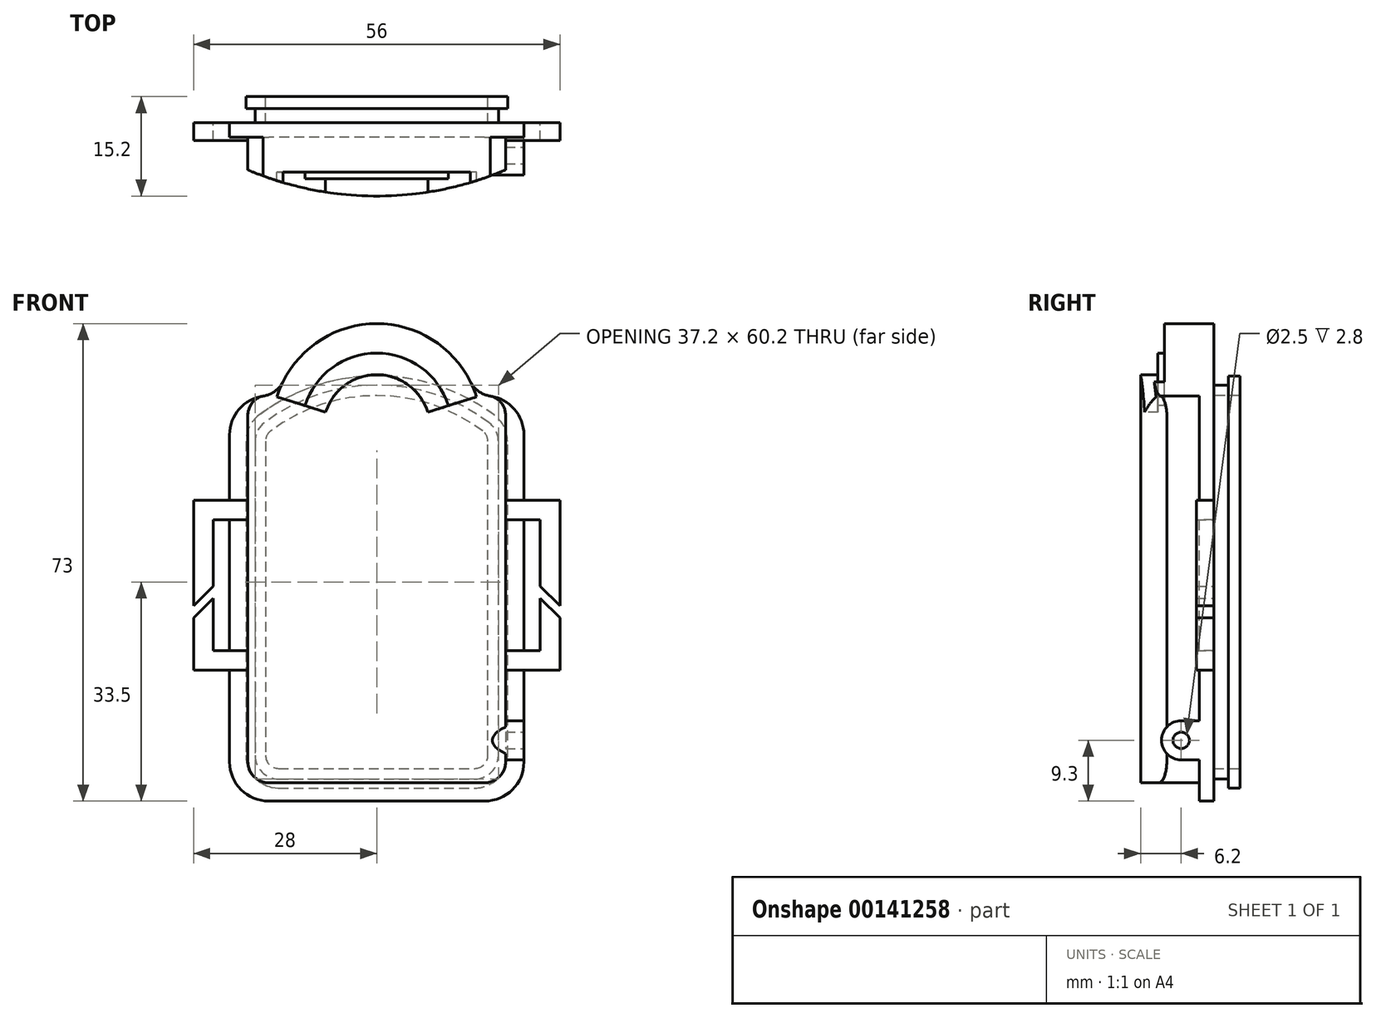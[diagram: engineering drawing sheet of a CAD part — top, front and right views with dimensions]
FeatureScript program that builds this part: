
annotation { "Feature Type Name" : "Feature", "Feature Type Description" : "" }
export const myFeature = defineFeature(function(context is Context, id is Id, definition is map)
    precondition{}
    {
        {
            var Q0;
            Q0=qCreatedBy(makeId("Front.planeOp"),FACE);
            var sketch = newSketch(context, id + "F0", { "sketchPlane" : qUnion([Q0])});
            skLineSegment(sketch, "E0.bottom", {"start": v(22.5, -57) * mm, "end": v(-22.5, -57) * mm});
            skLineSegment(sketch, "E0.top", {"start": v(22.5, 5) * mm, "end": v(-22.5, 5) * mm});
            skLineSegment(sketch, "E0.left", {"start": v(22.5, -57) * mm, "end": v(22.5, 5) * mm});
            skLineSegment(sketch, "E0.right", {"start": v(-22.5, -57) * mm, "end": v(-22.5, 5) * mm});
            skPoint(sketch, "E0.middle", {"position": v(0, -26) * mm});
            skArc(sketch, "E1", {"start": v(15.2, 5) * mm, "mid": v(0, 16) * mm, "end": v(-15.2, 5) * mm});
            skSolve(sketch);
        }
        {
            var Q0;
            Q0 = qSketchRegion(id + "F0", true);
            extrude(context, id + "F1", {"entities" : qUnion([Q0]), "depth" : 2.2 * mm});
        }
        {
            var Q0;
            Q0=makeQuery(id+"F1.opExtrude","SWEPT_EDGE",EDGE,{"disambiguationData":[OSD([sQuery(id+"F0.wireOp",EDGE,"E0.top"),sQuery(id+"F0.wireOp",EDGE,"E0.right")])]});
            var Q1;
            Q1=makeQuery(id+"F1.opExtrude","SWEPT_EDGE",EDGE,{"disambiguationData":[OSD([sQuery(id+"F0.wireOp",EDGE,"E0.top"),sQuery(id+"F0.wireOp",EDGE,"E0.left")])]});
            var Q2;
            Q2=makeQuery(id+"F1.opExtrude","SWEPT_EDGE",EDGE,{"disambiguationData":[OSD([sQuery(id+"F0.wireOp",EDGE,"E0.bottom"),sQuery(id+"F0.wireOp",EDGE,"E0.right")])]});
            var Q3;
            Q3=makeQuery(id+"F1.opExtrude","SWEPT_EDGE",EDGE,{"disambiguationData":[OSD([sQuery(id+"F0.wireOp",EDGE,"E0.bottom"),sQuery(id+"F0.wireOp",EDGE,"E0.left")])]});
            fillet(context, id + "F2", {"entities" : qUnion([Q0, Q1, Q2, Q3]), "radius" : 6 * mm, "allowEdgeOverflow" : false});
        }
        {
            var Q0;
            {var subQ0=sQuery(id+"F0.wireOp",EDGE,"E1");var subQ1=sQuery(id+"F0.wireOp",EDGE,"E0.top");Q0=makeQuery(id+"F1.opExtrude","SWEPT_EDGE",EDGE,{"disambiguationData":[OSD([subQ1,subQ0]),TDD([makeQuery(id+"F0.imprint","INTERSECT",VERTEX,{"disambiguationData":[OD(1.0)],"derivedFrom":[subQ1,subQ0]})])]});}
            var Q1;
            {var subQ0=sQuery(id+"F0.wireOp",EDGE,"E1");var subQ1=sQuery(id+"F0.wireOp",EDGE,"E0.top");Q1=makeQuery(id+"F1.opExtrude","SWEPT_EDGE",EDGE,{"disambiguationData":[OSD([subQ1,subQ0]),TDD([makeQuery(id+"F0.imprint","INTERSECT",VERTEX,{"disambiguationData":[OD(0.0)],"derivedFrom":[subQ1,subQ0]})])]});}
            fillet(context, id + "F3", {"entities" : qUnion([Q0, Q1]), "radius" : 4 * mm, "tangentPropagation" : true, "allowEdgeOverflow" : false});
        }
        {
            var Q0;
            Q0=makeQuery(id+"F1.opExtrude","CAP_FACE",FACE,{"disambiguationData":[OSD([sQuery(id+"F0.wireOp",EDGE,"E0.bottom"),sQuery(id+"F0.wireOp",EDGE,"E0.top"),sQuery(id+"F0.wireOp",EDGE,"E0.left"),sQuery(id+"F0.wireOp",EDGE,"E0.right"),sQuery(id+"F0.wireOp",EDGE,"E1")])],"isStart":false});
            var sketch = newSketch(context, id + "F4", { "sketchPlane" : qUnion([Q0])});
            skArc(sketch, "E2.0", {"start": v(22.5, -1) * mm, "mid": v(21.03, 2.93) * mm, "end": v(17.35, 4.94) * mm});
            skArc(sketch, "E3.0", {"start": v(-17.35, 4.94) * mm, "mid": v(-21.03, 2.93) * mm, "end": v(-22.5, -1) * mm});
            skArc(sketch, "E4.0", {"start": v(-14.33, 7.12) * mm, "mid": v(-15.57, 5.66) * mm, "end": v(-17.35, 4.94) * mm});
            skArc(sketch, "E5.0", {"start": v(14.33, 7.12) * mm, "mid": v(0, 16) * mm, "end": v(-14.33, 7.12) * mm});
            skArc(sketch, "E6.0", {"start": v(17.35, 4.94) * mm, "mid": v(15.57, 5.66) * mm, "end": v(14.33, 7.12) * mm});
            skLineSegment(sketch, "E7.0", {"start": v(-19.7, -51) * mm, "end": v(-19.7, 2.01) * mm});
            skLineSegment(sketch, "E7.1", {"start": v(19.7, -51) * mm, "end": v(19.7, 2.01) * mm});
            skArc(sketch, "E7.2", {"start": v(16.5, -54.2) * mm, "mid": v(18.76, -53.26) * mm, "end": v(19.7, -51) * mm});
            skLineSegment(sketch, "E7.3", {"start": v(16.5, -54.2) * mm, "end": v(-16.5, -54.2) * mm});
            skArc(sketch, "E7.4", {"start": v(-19.7, -51) * mm, "mid": v(-18.76, -53.26) * mm, "end": v(-16.5, -54.2) * mm});
            skArc(sketch, "E8", {"start": v(-19.7, 2.01) * mm, "mid": v(-19.04, 3.89) * mm, "end": v(-17.35, 4.94) * mm});
            skArc(sketch, "E9.MirrorCS", {"start": v(19.7, 2.01) * mm, "mid": v(19.04, 3.89) * mm, "end": v(17.35, 4.94) * mm});
            skSolve(sketch);
        }
        {
            var Q0;
            Q0=makeQuery(id+"F4.imprint","IMPRINT",FACE,{"disambiguationData":[TD([[makeQuery(id+"F4.imprint","IMPRINT",EDGE,{"derivedFrom":sQuery(id+"F4.wireOp",EDGE,"E4.0")}),1.0]])]});
            extrude(context, id + "F5", {"entities" : qUnion([Q0]), "operationType" : NewBodyOperationType.ADD, "depth" : 10 * mm});
        }
        {
            var Q0;
            Q0=qCreatedBy(makeId("Top.planeOp"),FACE);
            var sketch = newSketch(context, id + "F6", { "sketchPlane" : qUnion([Q0])});
            skLineSegment(sketch, "E10.0", {"start": v(19.7, -12.2) * mm, "end": v(19.7, -7.2) * mm});
            skLineSegment(sketch, "E11.0", {"start": v(-19.7, -12.2) * mm, "end": v(-19.7, -7.2) * mm});
            skArc(sketch, "E12", {"start": v(-19.7, -7.2) * mm, "mid": v(0, -11.2) * mm, "end": v(19.7, -7.2) * mm});
            skLineSegment(sketch, "E13", {"start": v(-19.7, -12.2) * mm, "end": v(19.7, -12.2) * mm});
            skPoint(sketch, "E14.orphan", {"position": v(-19.7, -2.2) * mm});
            skPoint(sketch, "E15.orphan", {"position": v(19.7, -2.2) * mm});
            skSolve(sketch);
        }
        {
            var Q0;
            Q0=makeQuery(id+"F6.imprint","IMPRINT",FACE,{"disambiguationData":[TD([[makeQuery(id+"F6.imprint","IMPRINT",EDGE,{"derivedFrom":sQuery(id+"F6.wireOp",EDGE,"E10.0")}),1.0]])]});
            extrude(context, id + "F7", {"entities" : qUnion([Q0]), "operationType" : NewBodyOperationType.REMOVE, "endBound" : BoundingType.THROUGH_ALL, "oppositeDirection" : true, "depth" : 25 * mm, "hasSecondDirection" : true, "secondDirectionBound" : SecondDirectionBoundingType.THROUGH_ALL, "secondDirectionOppositeDirection" : false, "secondDirectionDepth" : 25 * mm});
        }
        {
            var Q0;
            Q0=qCreatedBy(makeId("Right.planeOp"),FACE);
            var sketch = newSketch(context, id + "F8", { "sketchPlane" : qUnion([Q0])});
            skLineSegment(sketch, "E16", {"start": v(-11.2, 16) * mm, "end": v(0, 16) * mm});
            skLineSegment(sketch, "E17", {"start": v(-11.2, -54.2) * mm, "end": v(-11.2, 16) * mm});
            skLineSegment(sketch, "E18", {"start": v(-7.55, 16) * mm, "end": v(-7.55, 11.5) * mm});
            skLineSegment(sketch, "E19", {"start": v(-7.55, 11.5) * mm, "end": v(-8.55, 11.5) * mm});
            skLineSegment(sketch, "E20", {"start": v(-8.55, 11.5) * mm, "end": v(-8.55, 8.2) * mm});
            skLineSegment(sketch, "E21", {"start": v(-8.55, 8.2) * mm, "end": v(-11.2, 8.2) * mm});
            skLineSegment(sketch, "E22", {"start": v(-11.2, 16) * mm, "end": v(-11.2, 8.2) * mm});
            skLineSegment(sketch, "E23", {"start": v(0, 0) * mm, "end": v(-11.2, 0) * mm, "construction": true});
            skSolve(sketch);
        }
        {
            var Q0;
            {var subQ0=sQuery(id+"F8.wireOp",EDGE,"E18");Q0=makeQuery(id+"F8.imprint","IMPRINT",FACE,{"disambiguationData":[TD([[makeQuery(id+"F8.imprint","IMPRINT",EDGE,{"derivedFrom":subQ0}),-1.0]])]});}
            var Q1;
            Q1=sQuery(id+"F8.wireOp",EDGE,"E23");
            revolve(context, id + "F9", {"operationType" : NewBodyOperationType.REMOVE, "entities" : qUnion([Q0]), "axis" : qUnion([Q1]), "revolveType" : RevolveType.SYMMETRIC, "oppositeDirection" : true, "angle" : 145 * degree});
        }
        {
            var Q0;
            Q0=qCreatedBy(makeId("Front.planeOp"),FACE);
            var sketch = newSketch(context, id + "F10", { "sketchPlane" : qUnion([Q0])});
            skLineSegment(sketch, "E24.bottom", {"start": v(19.7, -11) * mm, "end": v(28, -11) * mm});
            skLineSegment(sketch, "E24.top", {"start": v(19.7, -37) * mm, "end": v(28, -37) * mm});
            skLineSegment(sketch, "E24.left", {"start": v(19.7, -11) * mm, "end": v(19.7, -14) * mm});
            skLineSegment(sketch, "E24.right", {"start": v(28, -11) * mm, "end": v(28, -27.16) * mm});
            skLineSegment(sketch, "E25.0", {"start": v(19.7, -34) * mm, "end": v(25, -34) * mm});
            skLineSegment(sketch, "E25.1", {"start": v(25, -14) * mm, "end": v(25, -24.16) * mm});
            skLineSegment(sketch, "E25.2", {"start": v(19.7, -14) * mm, "end": v(25, -14) * mm});
            skLineSegment(sketch, "E26", {"start": v(25, -26) * mm, "end": v(28, -29) * mm});
            skLineSegment(sketch, "E27", {"start": v(25, -24.16) * mm, "end": v(28, -27.16) * mm});
            skLineSegment(sketch, "E28.trimOffspring", {"start": v(19.7, -34) * mm, "end": v(19.7, -37) * mm});
            skLineSegment(sketch, "E29.trimOffspring", {"start": v(25, -26) * mm, "end": v(25, -34) * mm});
            skLineSegment(sketch, "E30.trimOffspring", {"start": v(28, -29) * mm, "end": v(28, -37) * mm});
            skLineSegment(sketch, "E31.MirrorCS", {"start": v(-19.7, -11) * mm, "end": v(-19.7, -14) * mm});
            skLineSegment(sketch, "E32.MirrorCS", {"start": v(-25, -24.16) * mm, "end": v(-28, -27.16) * mm});
            skLineSegment(sketch, "E33.MirrorCS", {"start": v(-19.7, -37) * mm, "end": v(-28, -37) * mm});
            skLineSegment(sketch, "E34.MirrorCS", {"start": v(-28, -11) * mm, "end": v(-28, -27.16) * mm});
            skLineSegment(sketch, "E35.MirrorCS", {"start": v(-19.7, -11) * mm, "end": v(-28, -11) * mm});
            skLineSegment(sketch, "E36.MirrorCS", {"start": v(-19.7, -34) * mm, "end": v(-19.7, -37) * mm});
            skLineSegment(sketch, "E37.MirrorCS", {"start": v(-25, -26) * mm, "end": v(-28, -29) * mm});
            skLineSegment(sketch, "E38.MirrorCS", {"start": v(-19.7, -34) * mm, "end": v(-25, -34) * mm});
            skLineSegment(sketch, "E39.MirrorCS", {"start": v(-28, -29) * mm, "end": v(-28, -37) * mm});
            skLineSegment(sketch, "E40.MirrorCS", {"start": v(-25, -26) * mm, "end": v(-25, -34) * mm});
            skLineSegment(sketch, "E41.MirrorCS", {"start": v(-25, -14) * mm, "end": v(-25, -24.16) * mm});
            skLineSegment(sketch, "E42.MirrorCS", {"start": v(-19.7, -14) * mm, "end": v(-25, -14) * mm});
            skSolve(sketch);
        }
        {
            var Q0;
            Q0 = qSketchRegion(id + "F10", true);
            extrude(context, id + "F11", {"entities" : qUnion([Q0]), "operationType" : NewBodyOperationType.ADD, "depth" : 2.7 * mm});
        }
        {
            var Q0;
            {var subQ2=sQuery(id+"F0.wireOp",EDGE,"E0.left");var subQ5=sQuery(id+"F10.wireOp",EDGE,"E24.top");Q0=makeQuery(id+"F11.boolean.opBoolean","SPLIT",FACE,{"disambiguationData":[TD([makeQuery(id+"F11.opExtrude","SWEPT_FACE",FACE,{"disambiguationData":[OSD([subQ5])]})])],"derivedFrom":makeQuery(id+"F1.opExtrude","SWEPT_FACE",FACE,{"disambiguationData":[OSD([subQ2])]})});}
            var sketch = newSketch(context, id + "F12", { "sketchPlane" : qUnion([Q0])});
            skLineSegment(sketch, "E43", {"start": v(0, -47.7) * mm, "end": v(-8.38, -47.7) * mm, "construction": true});
            skArc(sketch, "E44", {"start": v(-5, -44.7) * mm, "mid": v(-8, -47.7) * mm, "end": v(-5, -50.7) * mm});
            skCircle(sketch, "E45", {"center": v(-5, -47.7) * mm, "radius": 1.25 * mm});
            skLineSegment(sketch, "E46.bottom", {"start": v(-5, -50.7) * mm, "end": v(0, -50.7) * mm});
            skLineSegment(sketch, "E46.top", {"start": v(-5, -44.7) * mm, "end": v(0, -44.7) * mm});
            skLineSegment(sketch, "E46.right", {"start": v(0, -50.7) * mm, "end": v(0, -44.7) * mm});
            skSolve(sketch);
        }
        {
            var Q0;
            {var subQ1=sQuery(id+"F12.wireOp",EDGE,"E44");Q0=makeQuery(id+"F12.imprint","IMPRINT",FACE,{"disambiguationData":[TD([[makeQuery(id+"F12.imprint","IMPRINT",EDGE,{"derivedFrom":subQ1}),1.0]])]});}
            var Q1;
            {var subQ0=sQuery(id+"F12.wireOp",EDGE,"E46.right");Q1=makeQuery(id+"F12.imprint","IMPRINT",FACE,{"disambiguationData":[TD([[makeQuery(id+"F12.imprint","IMPRINT",EDGE,{"derivedFrom":subQ0}),1.0]])]});}
            var Q2;
            Q2=makeQuery(id+"F1.opExtrude","SWEPT_BODY",BODY,{"disambiguationData":[OSD([sQuery(id+"F0.wireOp",EDGE,"E0.bottom"),sQuery(id+"F0.wireOp",EDGE,"E0.top"),sQuery(id+"F0.wireOp",EDGE,"E0.left"),sQuery(id+"F0.wireOp",EDGE,"E0.right"),sQuery(id+"F0.wireOp",EDGE,"E1")])]});
            extrude(context, id + "F13", {"entities" : qUnion([Q0, Q1]), "operationType" : NewBodyOperationType.ADD, "endBound" : BoundingType.UP_TO_BODY, "oppositeDirection" : true, "endBoundEntityBody" : qUnion([Q2]), "depth" : 25 * mm});
        }
        {
            var Q0;
            Q0=makeQuery(id+"F11.boolean.opBoolean","MERGE",FACE,{"derivedFrom":[makeQuery(id+"F1.opExtrude","CAP_FACE",FACE,{"disambiguationData":[OSD([sQuery(id+"F0.wireOp",EDGE,"E0.bottom"),sQuery(id+"F0.wireOp",EDGE,"E0.top"),sQuery(id+"F0.wireOp",EDGE,"E0.left"),sQuery(id+"F0.wireOp",EDGE,"E0.right"),sQuery(id+"F0.wireOp",EDGE,"E1")])],"isStart":true}),makeQuery(id+"F11.opExtrude","CAP_FACE",FACE,{"disambiguationData":[OSD([sQuery(id+"F10.wireOp",EDGE,"E24.bottom"),sQuery(id+"F10.wireOp",EDGE,"E24.left"),sQuery(id+"F10.wireOp",EDGE,"E24.right"),sQuery(id+"F10.wireOp",EDGE,"E25.1"),sQuery(id+"F10.wireOp",EDGE,"E25.2"),sQuery(id+"F10.wireOp",EDGE,"E27")])],"isStart":true}),makeQuery(id+"F11.opExtrude","CAP_FACE",FACE,{"disambiguationData":[OSD([sQuery(id+"F10.wireOp",EDGE,"E24.top"),sQuery(id+"F10.wireOp",EDGE,"E25.0"),sQuery(id+"F10.wireOp",EDGE,"E26"),sQuery(id+"F10.wireOp",EDGE,"E28.trimOffspring"),sQuery(id+"F10.wireOp",EDGE,"E29.trimOffspring"),sQuery(id+"F10.wireOp",EDGE,"E30.trimOffspring")])],"isStart":true}),makeQuery(id+"F11.opExtrude","CAP_FACE",FACE,{"disambiguationData":[OSD([sQuery(id+"F10.wireOp",EDGE,"E31.MirrorCS"),sQuery(id+"F10.wireOp",EDGE,"E32.MirrorCS"),sQuery(id+"F10.wireOp",EDGE,"E34.MirrorCS"),sQuery(id+"F10.wireOp",EDGE,"E35.MirrorCS"),sQuery(id+"F10.wireOp",EDGE,"E41.MirrorCS"),sQuery(id+"F10.wireOp",EDGE,"E42.MirrorCS")])],"isStart":true}),makeQuery(id+"F11.opExtrude","CAP_FACE",FACE,{"disambiguationData":[OSD([sQuery(id+"F10.wireOp",EDGE,"E33.MirrorCS"),sQuery(id+"F10.wireOp",EDGE,"E36.MirrorCS"),sQuery(id+"F10.wireOp",EDGE,"E37.MirrorCS"),sQuery(id+"F10.wireOp",EDGE,"E38.MirrorCS"),sQuery(id+"F10.wireOp",EDGE,"E39.MirrorCS"),sQuery(id+"F10.wireOp",EDGE,"E40.MirrorCS")])],"isStart":true})]});
            var sketch = newSketch(context, id + "F14", { "sketchPlane" : qUnion([Q0])});
            skLineSegment(sketch, "E47", {"start": v(0, -55) * mm, "end": v(15, -55) * mm});
            skLineSegment(sketch, "E48", {"start": v(20, -50) * mm, "end": v(20, -2) * mm});
            skArc(sketch, "E49", {"start": v(18, 2) * mm, "mid": v(0, 8) * mm, "end": v(-18, 2) * mm});
            skLineSegment(sketch, "E50.MirrorCS", {"start": v(-20, -50) * mm, "end": v(-20, -2) * mm});
            skLineSegment(sketch, "E51.MirrorCS", {"start": v(0, -55) * mm, "end": v(-15, -55) * mm});
            skPoint(sketch, "E52.visualSharp", {"position": v(-20, -55) * mm});
            skArc(sketch, "E52.filletArc", {"start": v(-20, -50) * mm, "mid": v(-18.54, -53.54) * mm, "end": v(-15, -55) * mm});
            skPoint(sketch, "E53.visualSharp", {"position": v(20, -55) * mm});
            skArc(sketch, "E53.filletArc", {"start": v(15, -55) * mm, "mid": v(18.54, -53.54) * mm, "end": v(20, -50) * mm});
            skPoint(sketch, "E54.visualSharp", {"position": v(20, 0.36) * mm});
            skArc(sketch, "E54.filletArc", {"start": v(20, -2) * mm, "mid": v(19.47, 0.24) * mm, "end": v(18, 2) * mm});
            skPoint(sketch, "E55.visualSharp", {"position": v(-20, 0.36) * mm});
            skArc(sketch, "E55.filletArc", {"start": v(-18, 2) * mm, "mid": v(-19.47, 0.24) * mm, "end": v(-20, -2) * mm});
            skSolve(sketch);
        }
        {
            var Q0;
            Q0=qCreatedBy(makeId("Right.planeOp"),FACE);
            var sketch = newSketch(context, id + "F15", { "sketchPlane" : qUnion([Q0])});
            skLineSegment(sketch, "E56", {"start": v(0, -55) * mm, "end": v(0, -52) * mm});
            skLineSegment(sketch, "E57", {"start": v(0, -52) * mm, "end": v(4, -52) * mm});
            skLineSegment(sketch, "E58", {"start": v(4, -52) * mm, "end": v(4, -55) * mm});
            skLineSegment(sketch, "E59", {"start": v(4, -55) * mm, "end": v(2.2, -55) * mm});
            skLineSegment(sketch, "E60", {"start": v(2.2, -55) * mm, "end": v(2.2, -53.6) * mm});
            skLineSegment(sketch, "E61", {"start": v(2.2, -53.6) * mm, "end": v(0, -53.6) * mm});
            skSolve(sketch);
        }
        {
            var Q0;
            {var subQ0=sQuery(id+"F15.wireOp",EDGE,"E57");Q0=makeQuery(id+"F15.imprint","IMPRINT",FACE,{"disambiguationData":[TD([[makeQuery(id+"F15.imprint","IMPRINT",EDGE,{"derivedFrom":subQ0}),-1.0]])]});}
            var Q1;
            Q1=sQuery(id+"F14.wireOp",EDGE,"E47");
            var Q2;
            Q2=sQuery(id+"F14.wireOp",EDGE,"E53.filletArc");
            var Q3;
            Q3=sQuery(id+"F14.wireOp",EDGE,"E48");
            var Q4;
            Q4=sQuery(id+"F14.wireOp",EDGE,"E54.filletArc");
            var Q5;
            Q5=sQuery(id+"F14.wireOp",EDGE,"E49");
            var Q6;
            Q6=sQuery(id+"F14.wireOp",EDGE,"E55.filletArc");
            var Q7;
            Q7=sQuery(id+"F14.wireOp",EDGE,"E50.MirrorCS");
            var Q8;
            Q8=sQuery(id+"F14.wireOp",EDGE,"E52.filletArc");
            var Q9;
            Q9=sQuery(id+"F14.wireOp",EDGE,"E51.MirrorCS");
            sweep(context, id + "F16", {"operationType" : NewBodyOperationType.ADD, "profiles" : qUnion([Q0]), "path" : qUnion([Q1, Q2, Q3, Q4, Q5, Q6, Q7, Q8, Q9])});
        }
    });
